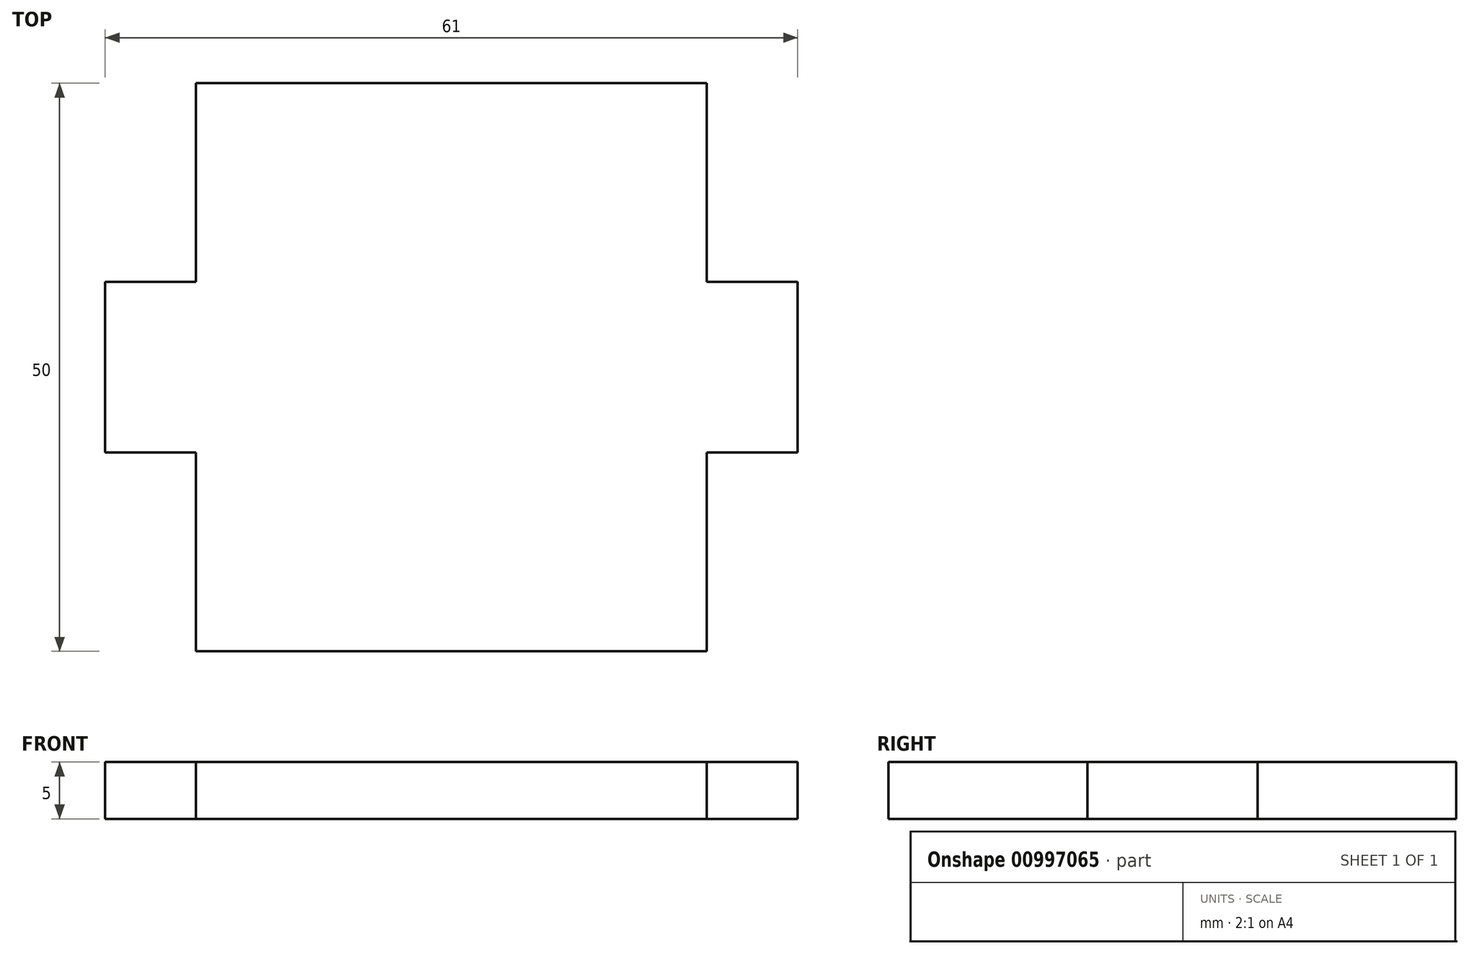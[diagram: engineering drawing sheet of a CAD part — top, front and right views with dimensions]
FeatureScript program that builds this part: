
annotation { "Feature Type Name" : "Feature", "Feature Type Description" : "" }
export const myFeature = defineFeature(function(context is Context, id is Id, definition is map)
    precondition{}
    {
        {
            var Q0;
            Q0=qCreatedBy(makeId("Top.planeOp"),FACE);
            var sketch = newSketch(context, id + "F0", { "sketchPlane" : qUnion([Q0])});
            skLineSegment(sketch, "E0", {"start": v(-30.5, 7.5) * mm, "end": v(-30.5, -7.5) * mm});
            skLineSegment(sketch, "E1", {"start": v(-30.5, -7.5) * mm, "end": v(-22.5, -7.5) * mm});
            skLineSegment(sketch, "E2", {"start": v(-22.5, -7.5) * mm, "end": v(-22.5, -25) * mm});
            skLineSegment(sketch, "E3", {"start": v(-22.5, -25) * mm, "end": v(0, -25) * mm});
            skLineSegment(sketch, "E4", {"start": v(0, -25) * mm, "end": v(0, 25) * mm});
            skLineSegment(sketch, "E5", {"start": v(0, 25) * mm, "end": v(-22.5, 25) * mm});
            skLineSegment(sketch, "E6", {"start": v(-22.5, 25) * mm, "end": v(-22.5, 7.5) * mm});
            skLineSegment(sketch, "E7", {"start": v(-22.5, 7.5) * mm, "end": v(-30.5, 7.5) * mm});
            skPoint(sketch, "E8", {"position": v(-30.5, 0) * mm});
            skPoint(sketch, "E9", {"position": v(0, 0) * mm});
            skLineSegment(sketch, "E10.MirrorCS", {"start": v(30.5, -7.5) * mm, "end": v(22.5, -7.5) * mm});
            skLineSegment(sketch, "E11.MirrorCS", {"start": v(22.5, 7.5) * mm, "end": v(30.5, 7.5) * mm});
            skLineSegment(sketch, "E12.MirrorCS", {"start": v(30.5, 7.5) * mm, "end": v(30.5, -7.5) * mm});
            skLineSegment(sketch, "E13.MirrorCS", {"start": v(22.5, -25) * mm, "end": v(0, -25) * mm});
            skLineSegment(sketch, "E14.MirrorCS", {"start": v(22.5, 25) * mm, "end": v(22.5, 7.5) * mm});
            skLineSegment(sketch, "E15.MirrorCS", {"start": v(0, 25) * mm, "end": v(22.5, 25) * mm});
            skLineSegment(sketch, "E16.MirrorCS", {"start": v(22.5, -7.5) * mm, "end": v(22.5, -25) * mm});
            skPoint(sketch, "E17.MirrorP", {"position": v(30.5, 0) * mm});
            skSolve(sketch);
        }
        {
            var Q0;
            Q0 = qSketchRegion(id + "F0", true);
            extrude(context, id + "F1", {"entities" : qUnion([Q0]), "depth" : 5 * mm, "offsetDistance" : 25 * mm});
        }
    });
